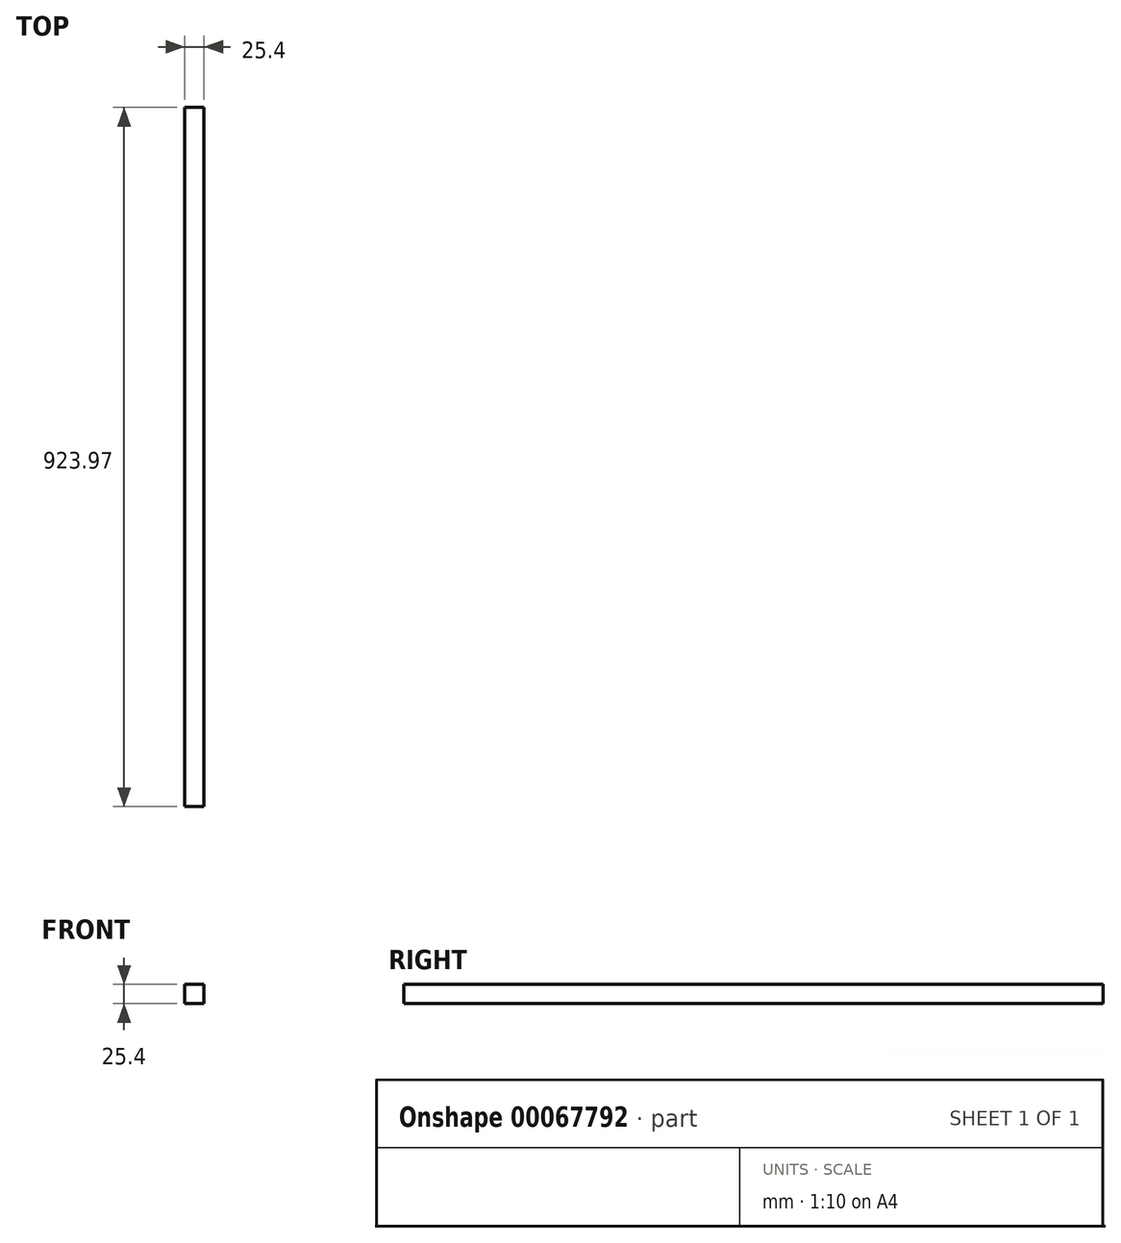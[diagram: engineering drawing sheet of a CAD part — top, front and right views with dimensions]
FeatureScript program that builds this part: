
annotation { "Feature Type Name" : "Feature", "Feature Type Description" : "" }
export const myFeature = defineFeature(function(context is Context, id is Id, definition is map)
    precondition{}
    {
        {
            var Q0;
            Q0=qCreatedBy(makeId("Front.planeOp"),FACE);
            var sketch = newSketch(context, id + "F0", { "sketchPlane" : qUnion([Q0])});
            skLineSegment(sketch, "E0.bottom", {"start": v(-72.77, 25.4) * mm, "end": v(-47.37, 25.4) * mm});
            skLineSegment(sketch, "E0.top", {"start": v(-72.77, 0) * mm, "end": v(-47.37, 0) * mm});
            skLineSegment(sketch, "E0.left", {"start": v(-72.77, 25.4) * mm, "end": v(-72.77, 0) * mm});
            skLineSegment(sketch, "E0.right", {"start": v(-47.37, 25.4) * mm, "end": v(-47.37, 0) * mm});
            skSolve(sketch);
        }
        {
            var Q0;
            Q0=makeQuery(id+"F0.imprint","IMPRINT",FACE,{"disambiguationData":[TD([[makeQuery(id+"F0.imprint","IMPRINT",EDGE,{"derivedFrom":sQuery(id+"F0.wireOp",EDGE,"E0.bottom")}),-1.0]])]});
            extrude(context, id + "F1", {"entities" : qUnion([Q0]), "depth" : 508 * mm, "hasSecondDirection" : true, "secondDirectionOppositeDirection" : true, "secondDirectionDepth" : 415.97 * mm});
        }
    });
